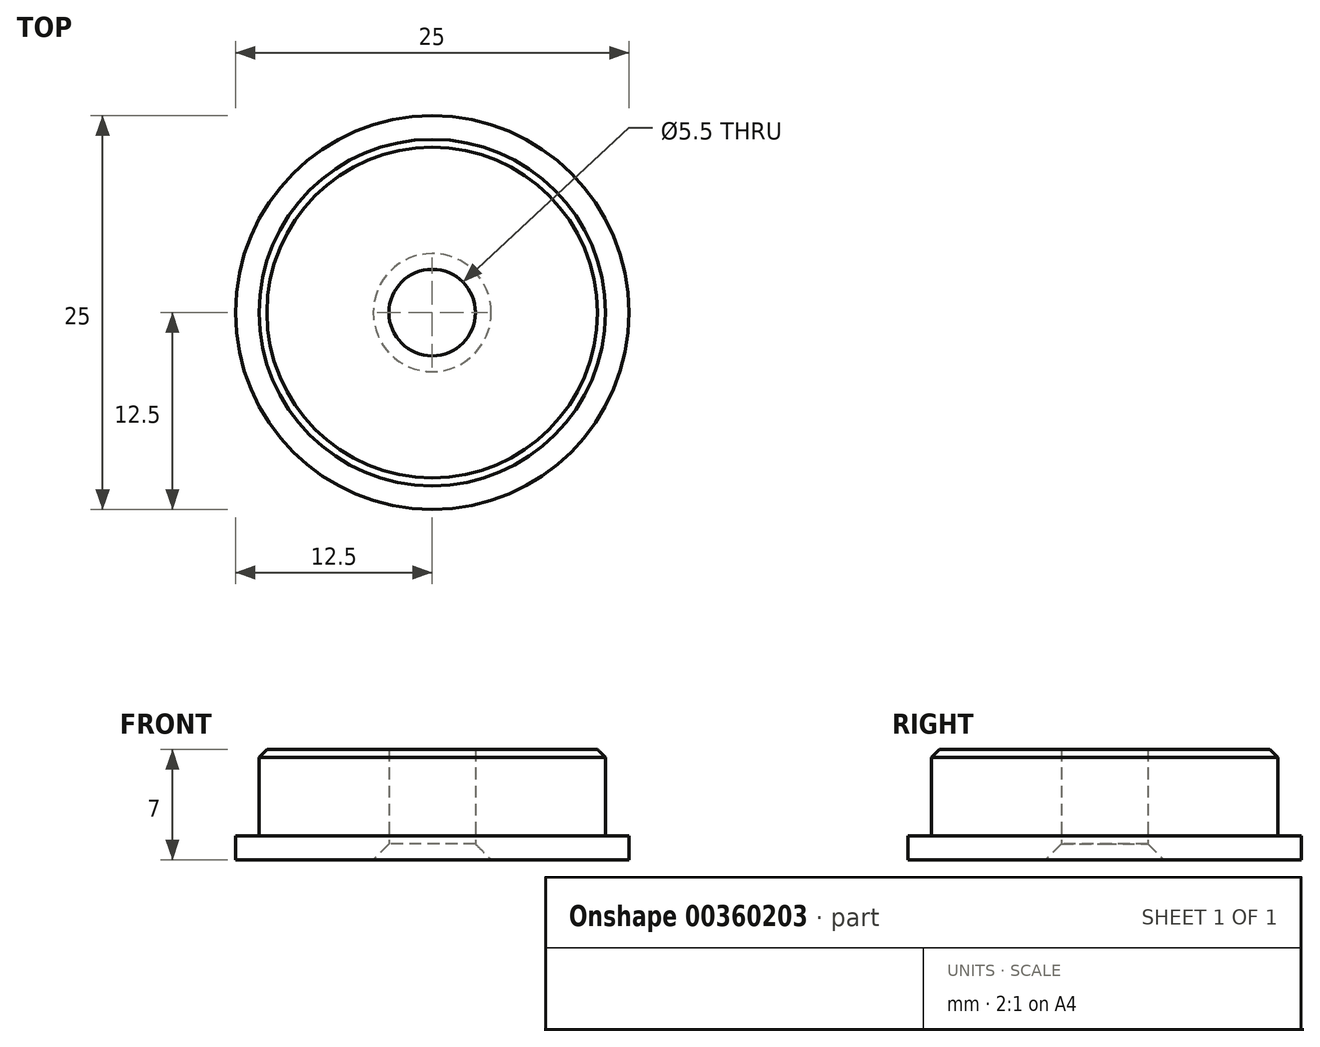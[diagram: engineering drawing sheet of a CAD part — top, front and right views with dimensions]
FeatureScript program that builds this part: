
annotation { "Feature Type Name" : "Feature", "Feature Type Description" : "" }
export const myFeature = defineFeature(function(context is Context, id is Id, definition is map)
    precondition{}
    {
        {
            var Q0;
            Q0=qCreatedBy(makeId("Top.planeOp"),FACE);
            var sketch = newSketch(context, id + "F0", { "sketchPlane" : qUnion([Q0])});
            skCircle(sketch, "E0", {"center": v(0, 0) * mm, "radius": 2.75 * mm});
            skCircle(sketch, "E1.0", {"center": v(0, 0) * mm, "radius": 11 * mm});
            skCircle(sketch, "E2", {"center": v(0, 0) * mm, "radius": 12.5 * mm});
            skSolve(sketch);
        }
        {
            var Q0;
            Q0=makeQuery(id+"F0.imprint","IMPRINT",FACE,{"disambiguationData":[TD([[makeQuery(id+"F0.imprint","IMPRINT",EDGE,{"derivedFrom":sQuery(id+"F0.wireOp",EDGE,"E0")}),-1.0]])]});
            extrude(context, id + "F1", {"entities" : qUnion([Q0]), "depth" : 7 * mm, "offsetDistance" : 25 * mm});
        }
        {
            var Q0;
            Q0=makeQuery(id+"F0.imprint","IMPRINT",FACE,{"disambiguationData":[TD([[makeQuery(id+"F0.imprint","IMPRINT",EDGE,{"derivedFrom":sQuery(id+"F0.wireOp",EDGE,"E1.0")}),-1.0]])]});
            extrude(context, id + "F2", {"entities" : qUnion([Q0]), "operationType" : NewBodyOperationType.ADD, "depth" : 1.5 * mm, "offsetDistance" : 25 * mm});
        }
        {
            var Q0;
            Q0=makeQuery(id+"F1.opExtrude","CAP_EDGE",EDGE,{"disambiguationData":[OSD([sQuery(id+"F0.wireOp",EDGE,"E1.0")])],"isStart":false});
            chamfer(context, id + "F3", {"entities" : qUnion([Q0]), "width" : 0.5 * mm, "tangentPropagation" : true});
        }
        {
            var Q0;
            Q0=makeQuery(id+"F1.opExtrude","CAP_EDGE",EDGE,{"disambiguationData":[OSD([sQuery(id+"F0.wireOp",EDGE,"E0")])],"isStart":true});
            chamfer(context, id + "F4", {"entities" : qUnion([Q0]), "width" : 1 * mm, "tangentPropagation" : true});
        }
    });
